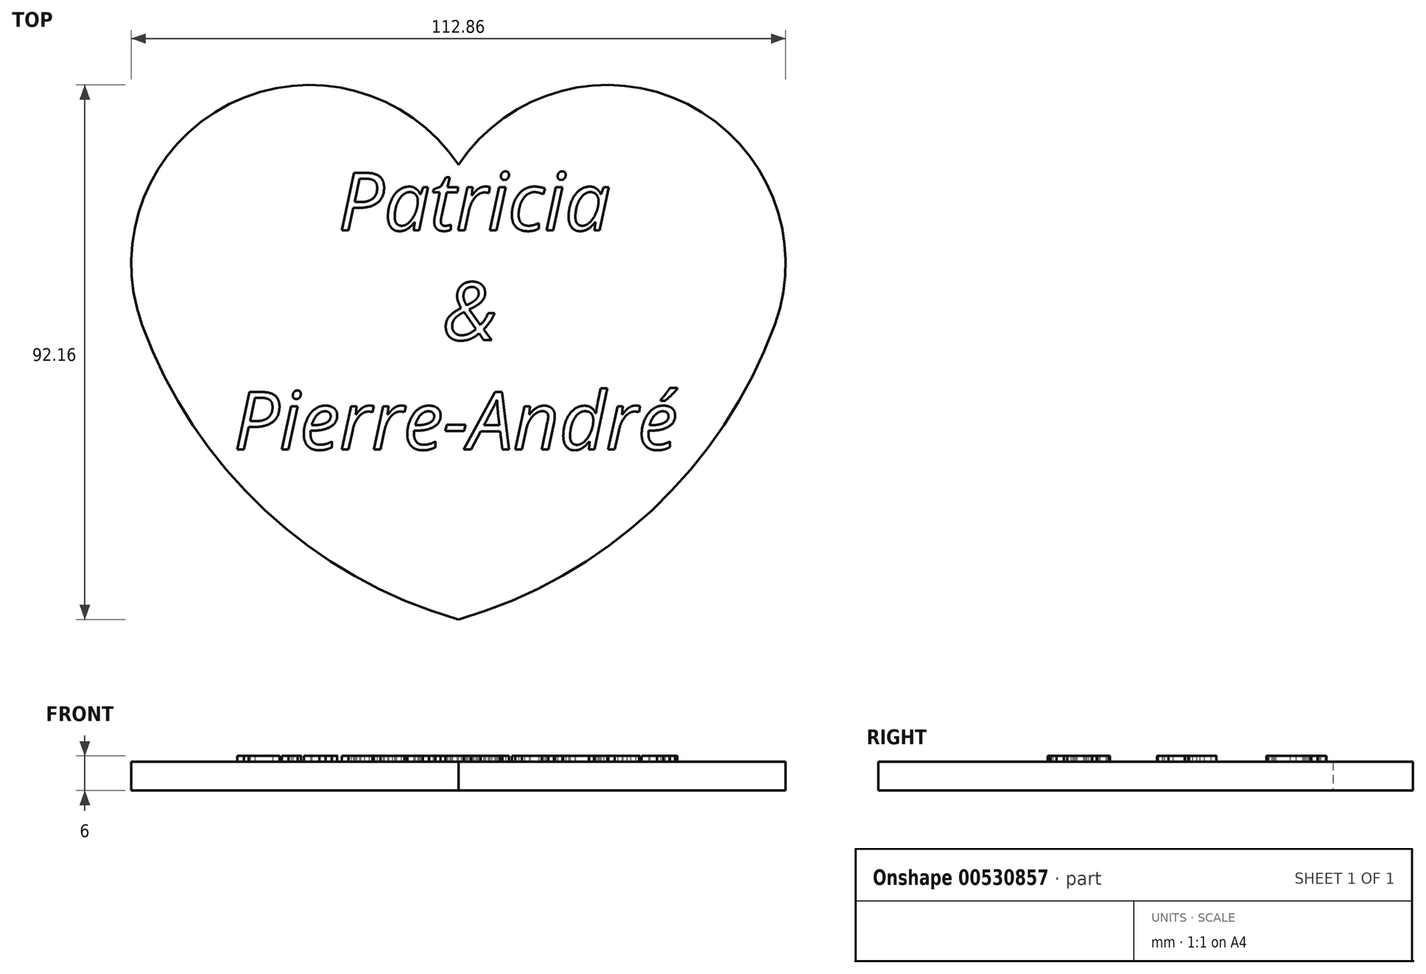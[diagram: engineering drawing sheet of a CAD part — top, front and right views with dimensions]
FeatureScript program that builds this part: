
annotation { "Feature Type Name" : "Feature", "Feature Type Description" : "" }
export const myFeature = defineFeature(function(context is Context, id is Id, definition is map)
    precondition{}
    {
        {
            var Q0;
            Q0=qCreatedBy(makeId("Top.planeOp"),FACE);
            var sketch = newSketch(context, id + "F0", { "sketchPlane" : qUnion([Q0])});
            skArc(sketch, "E0", {"start": v(0, 27.52) * mm, "mid": v(-39.5, 38) * mm, "end": v(-54.57, 0) * mm});
            skArc(sketch, "E1", {"start": v(-54.57, 0) * mm, "mid": v(-33.4, -32) * mm, "end": v(0, -50.87) * mm});
            skArc(sketch, "E2.MirrorCS", {"start": v(0, 27.52) * mm, "mid": v(39.5, 38) * mm, "end": v(54.57, 0) * mm});
            skArc(sketch, "E3.MirrorCS", {"start": v(54.57, 0) * mm, "mid": v(33.4, -32) * mm, "end": v(0, -50.87) * mm});
            skSolve(sketch);
        }
        {
            var Q0;
            Q0=makeQuery(id+"F0.imprint","IMPRINT",FACE,{"disambiguationData":[TD([[makeQuery(id+"F0.imprint","IMPRINT",EDGE,{"derivedFrom":sQuery(id+"F0.wireOp",EDGE,"E0")}),1.0]])]});
            extrude(context, id + "F1", {"entities" : qUnion([Q0]), "depth" : 5 * mm, "offsetDistance" : 25 * mm});
        }
        {
            var Q0;
            Q0=makeQuery(id+"F1.opExtrude","CAP_FACE",FACE,{"disambiguationData":[OSD([sQuery(id+"F0.wireOp",EDGE,"E0"),sQuery(id+"F0.wireOp",EDGE,"E1"),sQuery(id+"F0.wireOp",EDGE,"E2.MirrorCS"),sQuery(id+"F0.wireOp",EDGE,"E3.MirrorCS")])],"isStart":false});
            var sketch = newSketch(context, id + "F2", { "sketchPlane" : qUnion([Q0])});
            skText(sketch, "E4", { "text": "     Patricia\n          & \nPierre-André", "fontName": "OpenSans-Italic.ttf"});
            const initialGuessF2  = {"E4": [-0.03872, 0.01621, 1, 0, 0.01]};
            skSetInitialGuess(sketch, initialGuessF2);
            skSolve(sketch);
        }
        {
            var Q0;
            Q0 = qSketchRegion(id + "F2", true);
            extrude(context, id + "F3", {"entities" : qUnion([Q0]), "operationType" : NewBodyOperationType.ADD, "depth" : 1 * mm, "offsetDistance" : 25 * mm});
        }
    });
